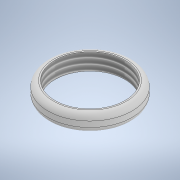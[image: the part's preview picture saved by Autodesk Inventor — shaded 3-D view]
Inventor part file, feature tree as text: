
AUTODESK INVENTOR PART (.ipt)
format: ipt  version: 2021 (Build 250183000, 183)  size: 145,408 bytes
history: native  units: mm
features: extrude x2, sketch x2, fillet x1, other x1
ambient origin geometry x8: Origin, YZ Plane, XZ Plane, XY Plane, X Axis, Y Axis, Z Axis, Center Point
bodies: Body1 (feature_tree)
feature tree (6):
  extrude  "Extrusion1"  Depth=30.0mm
  fillet  "Congé1"  Radius=6.0mm
  extrude  "Extrusion2"  Depth=2.0mm
  other  "Filetage2"
  sketch  "Esquisse1"
  sketch  "Esquisse2"
